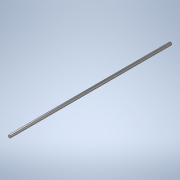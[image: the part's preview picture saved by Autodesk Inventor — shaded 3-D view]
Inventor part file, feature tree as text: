
AUTODESK INVENTOR PART (.ipt)
format: ipt  version: 2020 (Build 240168000, 168)  size: 109,568 bytes
history: native  units: in
note: dims shown in document units (in); Inventor stores cm internally (conversion verified against a paired STEP export)
features: extrude x1, sketch x1
ambient origin geometry x8: Origin, YZ Plane, XZ Plane, XY Plane, X Axis, Y Axis, Z Axis, Center Point
bodies: Solid1 (feature_tree)
feature tree (2):
  extrude  "Extrusion1"  Depth=34.0in TaperAngle=0.0deg
  sketch  "Sketch1"  dims[d0=0.5in d1=34.0in d2=0.0in]
